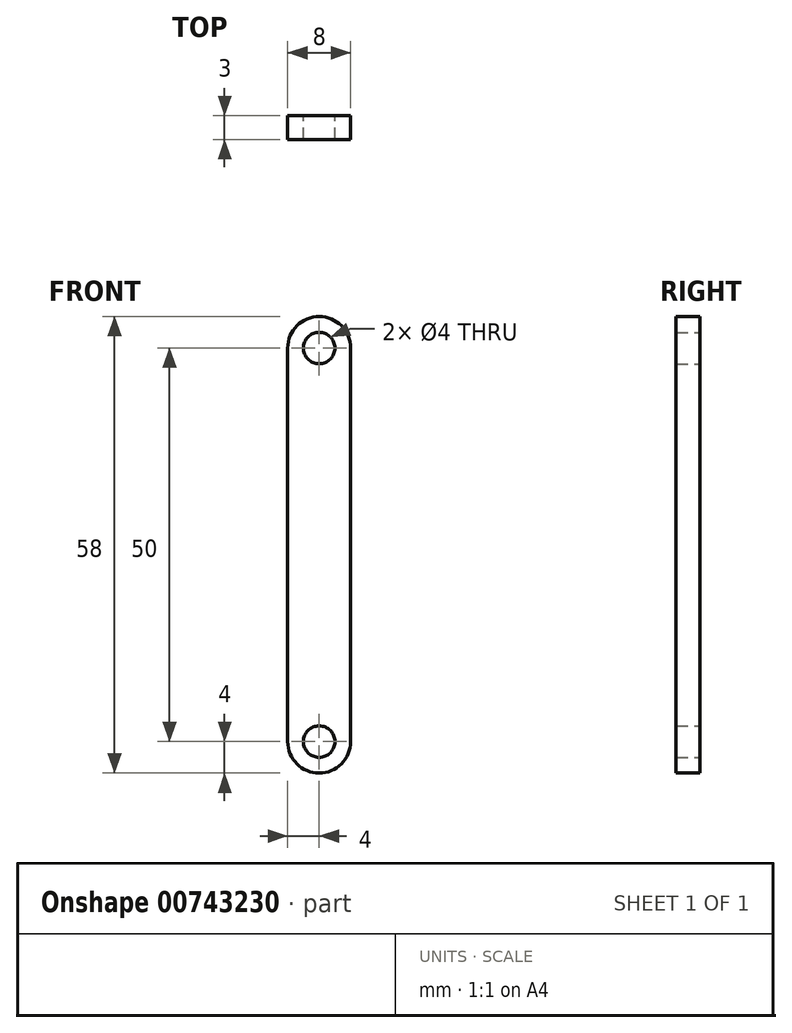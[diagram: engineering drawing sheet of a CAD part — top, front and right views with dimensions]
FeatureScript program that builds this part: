
annotation { "Feature Type Name" : "Feature", "Feature Type Description" : "" }
export const myFeature = defineFeature(function(context is Context, id is Id, definition is map)
    precondition{}
    {
        {
            var Q0;
            Q0=qCreatedBy(makeId("Front.planeOp"),FACE);
            var sketch = newSketch(context, id + "F0", { "sketchPlane" : qUnion([Q0])});
            skLineSegment(sketch, "E0.bottom", {"start": v(4, 25) * mm, "end": v(-4, 25) * mm, "construction": true});
            skLineSegment(sketch, "E0.top", {"start": v(4, -25) * mm, "end": v(-4, -25) * mm, "construction": true});
            skLineSegment(sketch, "E0.left", {"start": v(4, 25) * mm, "end": v(4, -25) * mm});
            skLineSegment(sketch, "E0.right", {"start": v(-4, 25) * mm, "end": v(-4, -25) * mm});
            skPoint(sketch, "E0.middle", {"position": v(0, 0) * mm});
            skArc(sketch, "E1", {"start": v(4, 25) * mm, "mid": v(0, 29) * mm, "end": v(-4, 25) * mm});
            skArc(sketch, "E2", {"start": v(-4, -25) * mm, "mid": v(0, -29) * mm, "end": v(4, -25) * mm});
            skCircle(sketch, "E3", {"center": v(0, 25) * mm, "radius": 2 * mm});
            skCircle(sketch, "E4", {"center": v(0, -25) * mm, "radius": 2 * mm});
            skSolve(sketch);
        }
        {
            var Q0;
            Q0=qSketchRegion(id+"F0",true);
            extrude(context, id + "F1", {"entities" : qUnion([Q0]), "depth" : 3 * mm, "offsetDistance" : 25 * mm});
        }
    });
